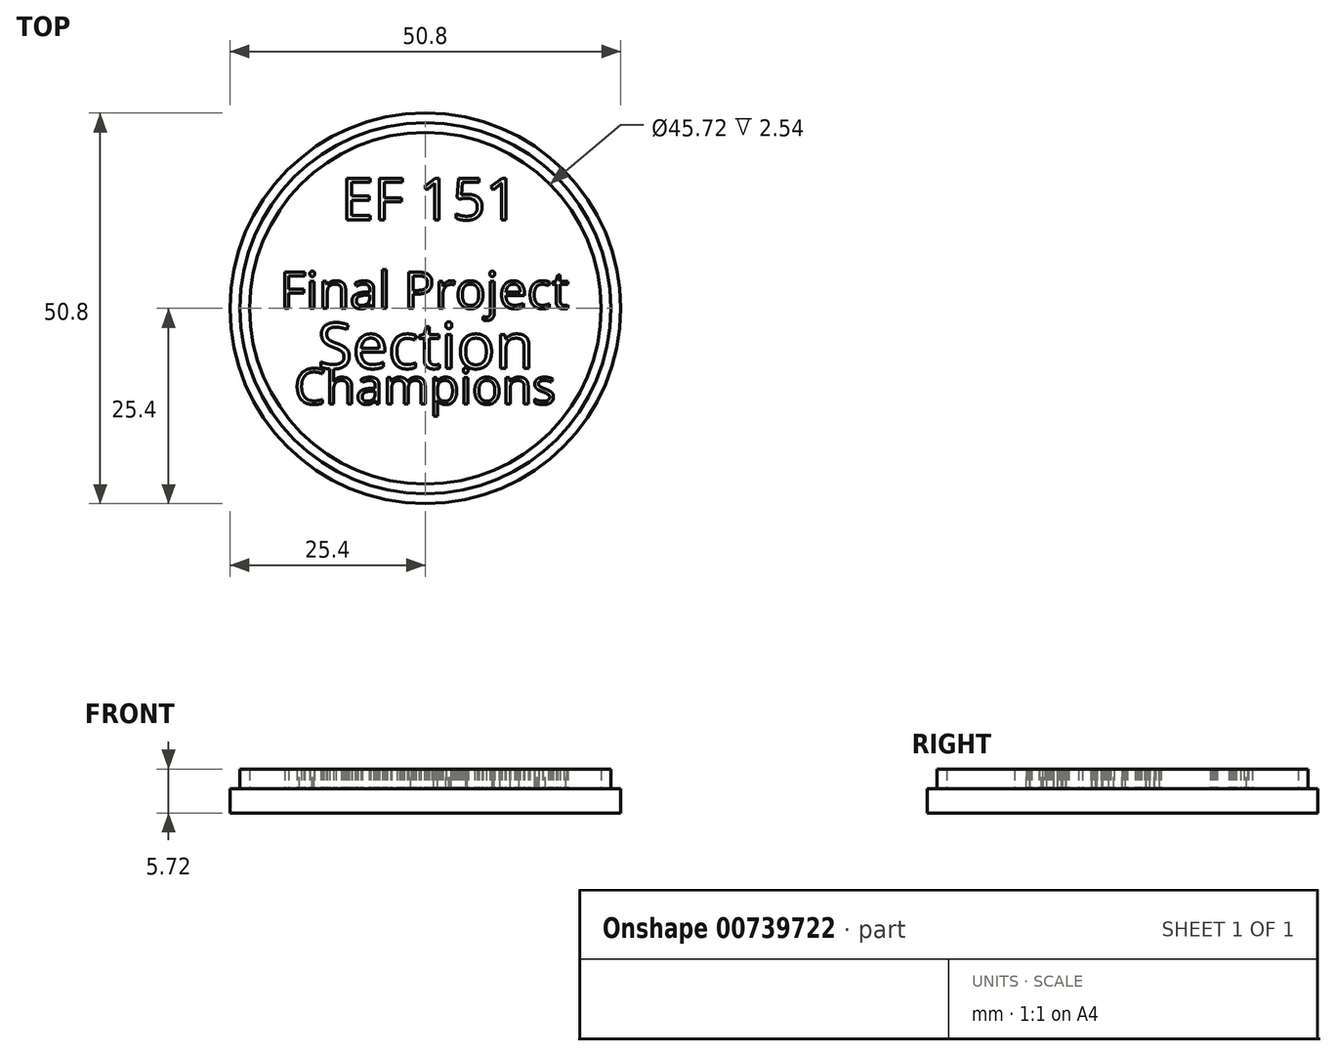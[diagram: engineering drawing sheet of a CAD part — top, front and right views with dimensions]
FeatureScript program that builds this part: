
annotation { "Feature Type Name" : "Feature", "Feature Type Description" : "" }
export const myFeature = defineFeature(function(context is Context, id is Id, definition is map)
    precondition{}
    {
        {
            var Q0;
            Q0=qCreatedBy(makeId("Top.planeOp"),FACE);
            var sketch = newSketch(context, id + "F0", { "sketchPlane" : qUnion([Q0])});
            skCircle(sketch, "E0", {"center": v(0, 0) * mm, "radius": 25.4 * mm});
            skSolve(sketch);
        }
        {
            var Q0;
            Q0=makeQuery(id+"F0.imprint","IMPRINT",FACE,{"disambiguationData":[TD([[makeQuery(id+"F0.imprint","IMPRINT",EDGE,{"derivedFrom":sQuery(id+"F0.wireOp",EDGE,"E0")}),1.0]])]});
            extrude(context, id + "F1", {"entities" : qUnion([Q0]), "depth" : 3.17 * mm, "offsetDistance" : 25.4 * mm});
        }
        {
            var Q0;
            Q0=makeQuery(id+"F1.opExtrude","CAP_FACE",FACE,{"disambiguationData":[OSD([sQuery(id+"F0.wireOp",EDGE,"E0")])],"isStart":false});
            var sketch = newSketch(context, id + "F2", { "sketchPlane" : qUnion([Q0])});
            skCircle(sketch, "E1", {"center": v(0, 0) * mm, "radius": 24.13 * mm});
            skCircle(sketch, "E2", {"center": v(0, 0) * mm, "radius": 22.86 * mm});
            skSolve(sketch);
        }
        {
            var Q0;
            Q0=makeQuery(id+"F2.imprint","IMPRINT",FACE,{"disambiguationData":[TD([[makeQuery(id+"F2.imprint","IMPRINT",EDGE,{"derivedFrom":sQuery(id+"F2.wireOp",EDGE,"E1")}),1.0]])]});
            extrude(context, id + "F3", {"entities" : qUnion([Q0]), "operationType" : NewBodyOperationType.ADD, "depth" : 2.54 * mm, "offsetDistance" : 25.4 * mm});
        }
        {
            var Q0;
            Q0=makeQuery(id+"F3.boolean.opBoolean","SPLIT",FACE,{"disambiguationData":[TD([makeQuery(id+"F3.opExtrude","SWEPT_FACE",FACE,{"disambiguationData":[OSD([sQuery(id+"F2.wireOp",EDGE,"E2")])]})])],"derivedFrom":makeQuery(id+"F1.opExtrude","CAP_FACE",FACE,{"disambiguationData":[OSD([sQuery(id+"F0.wireOp",EDGE,"E0")])],"isStart":false})});
            var sketch = newSketch(context, id + "F4", { "sketchPlane" : qUnion([Q0])});
            skText(sketch, "E3", { "text": "EF 151", "fontName": "OpenSans-Regular.ttf"});
            skText(sketch, "E4", { "text": "Final Project", "fontName": "OpenSans-Regular.ttf"});
            skText(sketch, "E5", { "text": "Section\n", "fontName": "OpenSans-Regular.ttf"});
            skText(sketch, "E6", { "text": "Champions", "fontName": "OpenSans-Regular.ttf"});
            const initialGuessF4  = {"E3": [-0.01095, 0.01152, 1, 0, 0.00546], "E4": [-0.01896, 0, 1, 0, 0.00475], "E5": [-0.01403, -0.00782, 1, 0, 0.00595], "E6": [-0.01707, -0.01245, 1, 0, 0.00463]};
            skSetInitialGuess(sketch, initialGuessF4);
            skSolve(sketch);
        }
        {
            var Q0;
            Q0 = qSketchRegion(id + "F4", true);
            extrude(context, id + "F5", {"entities" : qUnion([Q0]), "operationType" : NewBodyOperationType.ADD, "depth" : 2.54 * mm, "offsetDistance" : 25.4 * mm});
        }
    });
